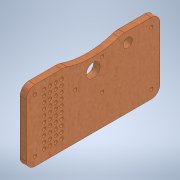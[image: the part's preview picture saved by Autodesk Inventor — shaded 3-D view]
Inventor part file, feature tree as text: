
AUTODESK INVENTOR PART (.ipt)
format: ipt  version: 2020.3 (Build 243373000, 373)  size: 248,832 bytes
history: native  units: mm
features: sketch x7, hole x4, extrude x3, fillet x2, other x1
ambient origin geometry x8: Origin, YZ Plane, XZ Plane, XY Plane, X Axis, Y Axis, Z Axis, Center Point
bodies: Body1 (feature_tree)
feature tree (17):
  other  "ソリッド1"
  extrude  "押し出し1"  Depth=61.5mm
  hole  "穴1"  [1 undecoded]
  fillet  "フィレット1"  Radius=5.5mm
  hole  "穴2"  [1 undecoded]
  hole  "穴3"  [1 undecoded]
  extrude  "押し出し2"  Depth=7.5mm
  fillet  "フィレット2"  Radius=7.5mm
  hole  "穴4"  [1 undecoded]
  extrude  "押し出し3"  Depth=7.5mm
  sketch  "スケッチ1"
  sketch  "スケッチ2"
  sketch  "スケッチ3"
  sketch  "スケッチ4"
  sketch  "スケッチ5"
  sketch  "スケッチ6"
  sketch  "スケッチ7"
note: 4 required parameter values undecoded (feature->parameter linkage not recoverable at this tier; creation-order binding heuristic only, values carry confidence <= 0.55)
